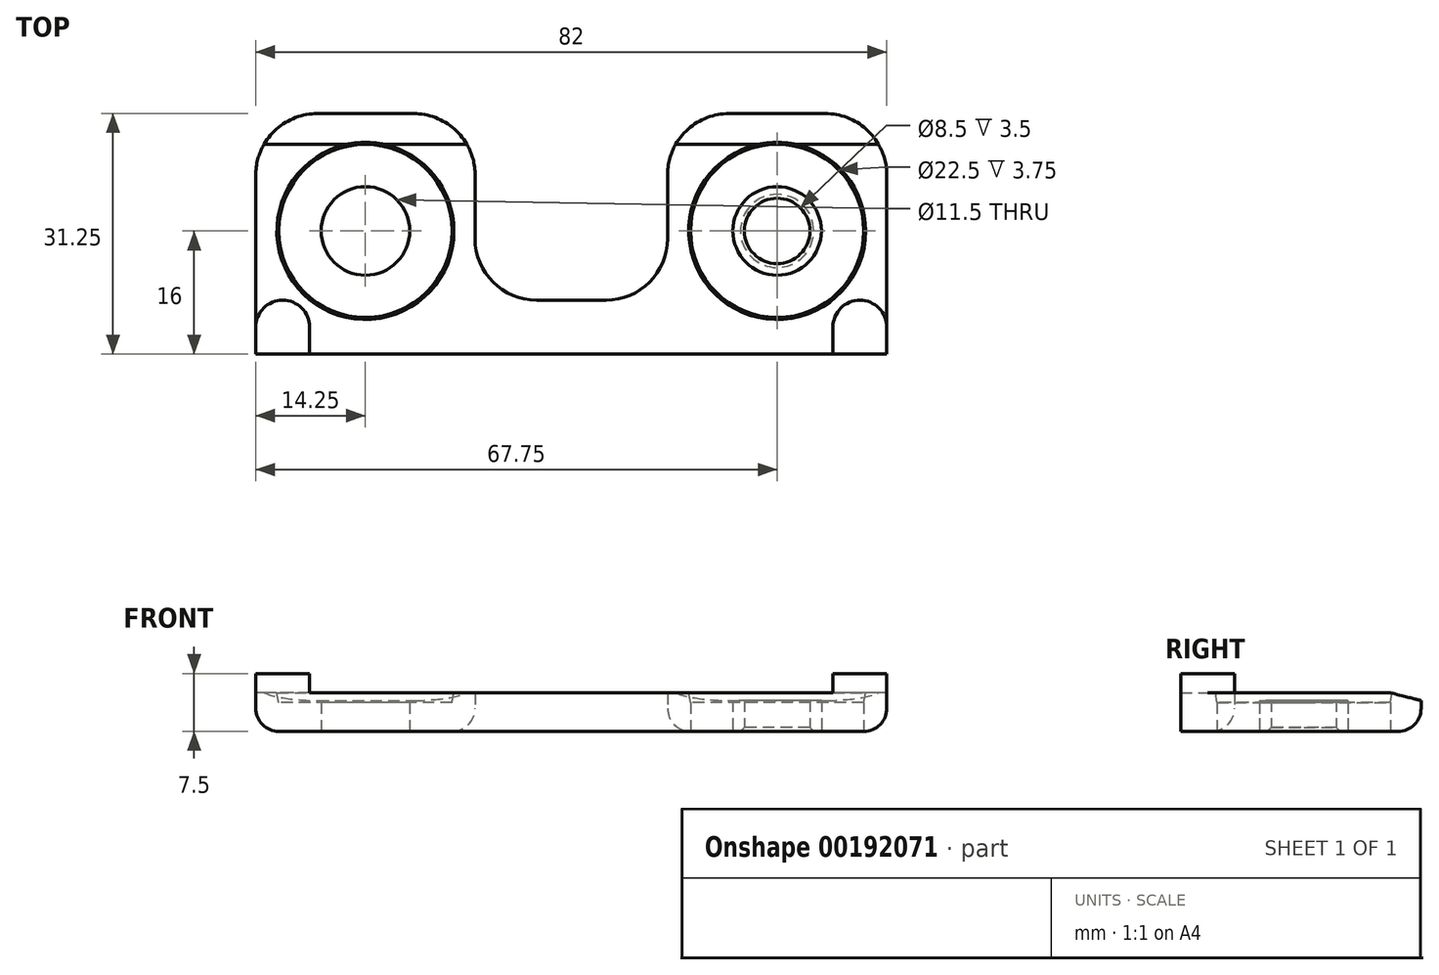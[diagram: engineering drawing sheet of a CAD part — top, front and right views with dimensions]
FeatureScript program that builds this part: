
annotation { "Feature Type Name" : "Feature", "Feature Type Description" : "" }
export const myFeature = defineFeature(function(context is Context, id is Id, definition is map)
    precondition{}
    {
        {
            var Q0;
            Q0=qCreatedBy(makeId("Top.planeOp"),FACE);
            var sketch = newSketch(context, id + "F0", { "sketchPlane" : qUnion([Q0])});
            skLineSegment(sketch, "E0.bottom", {"start": v(41, -3.5) * mm, "end": v(-41, -3.5) * mm});
            skLineSegment(sketch, "E0.top", {"start": v(12.5, 3.5) * mm, "end": v(-12.5, 3.5) * mm});
            skLineSegment(sketch, "E0.left", {"start": v(41, -3.5) * mm, "end": v(41, 3.5) * mm});
            skLineSegment(sketch, "E0.right", {"start": v(-41, -3.5) * mm, "end": v(-41, 3.5) * mm});
            skPoint(sketch, "E0.middle", {"position": v(0, 0) * mm});
            skLineSegment(sketch, "E1", {"start": v(-41, 3.5) * mm, "end": v(-41, 27.75) * mm});
            skLineSegment(sketch, "E2", {"start": v(-41, 27.75) * mm, "end": v(-12.5, 27.75) * mm});
            skLineSegment(sketch, "E3", {"start": v(-12.5, 27.75) * mm, "end": v(-12.5, 3.5) * mm});
            skCircle(sketch, "E4", {"center": v(-26.75, 12.5) * mm, "radius": 4.25 * mm});
            skLineSegment(sketch, "E5", {"start": v(-26.75, 18.7) * mm, "end": v(-26.75, 6.28) * mm, "construction": true});
            skLineSegment(sketch, "E6", {"start": v(0, -8.57) * mm, "end": v(0, 17) * mm, "construction": true});
            skLineSegment(sketch, "E7.MirrorCS", {"start": v(-41, 27.75) * mm, "end": v(-41, 3.5) * mm});
            skLineSegment(sketch, "E8.MirrorCS", {"start": v(-12.5, 3.5) * mm, "end": v(-12.5, 27.75) * mm});
            skLineSegment(sketch, "E9.MirrorCS", {"start": v(-12.5, 27.75) * mm, "end": v(-41, 27.75) * mm});
            skLineSegment(sketch, "E10.MirrorCS", {"start": v(12.5, 27.75) * mm, "end": v(12.5, 3.5) * mm});
            skCircle(sketch, "E11.MirrorC", {"center": v(26.75, 12.5) * mm, "radius": 4.25 * mm});
            skLineSegment(sketch, "E12.MirrorCS", {"start": v(12.5, 27.75) * mm, "end": v(41, 27.75) * mm});
            skLineSegment(sketch, "E13.MirrorCS", {"start": v(41, 27.75) * mm, "end": v(41, 3.5) * mm});
            skCircle(sketch, "E14", {"center": v(-26.75, 12.5) * mm, "radius": 11.25 * mm});
            skCircle(sketch, "E15.MirrorC", {"center": v(26.75, 12.5) * mm, "radius": 11.25 * mm});
            skCircle(sketch, "E16.0", {"center": v(-26.75, 12.5) * mm, "radius": 5.75 * mm});
            skCircle(sketch, "E17.MirrorC", {"center": v(26.75, 12.5) * mm, "radius": 5.75 * mm});
            skLineSegment(sketch, "E18", {"start": v(-41, 3.5) * mm, "end": v(-34, 3.5) * mm});
            skLineSegment(sketch, "E19", {"start": v(-34, 3.5) * mm, "end": v(-34, -3.5) * mm});
            skLineSegment(sketch, "E20.MirrorCS", {"start": v(34, 3.5) * mm, "end": v(34, -3.5) * mm});
            skLineSegment(sketch, "E21.MirrorCS", {"start": v(41, 3.5) * mm, "end": v(34, 3.5) * mm});
            skSolve(sketch);
        }
        {
            var Q0;
            Q0=makeQuery(id+"F0.imprint","IMPRINT",FACE,{"disambiguationData":[TD([[makeQuery(id+"F0.imprint","IMPRINT",EDGE,{"derivedFrom":sQuery(id+"F0.wireOp",EDGE,"E0.bottom")}),-1.0]])]});
            var Q1;
            Q1=makeQuery(id+"F0.imprint","IMPRINT",FACE,{"disambiguationData":[TD([[makeQuery(id+"F0.imprint","IMPRINT",EDGE,{"derivedFrom":sQuery(id+"F0.wireOp",EDGE,"E0.top")}),1.0]])]});
            extrude(context, id + "F1", {"entities" : qUnion([Q0, Q1]), "depth" : 5 * mm});
        }
        {
            var Q0;
            Q0=makeQuery(id+"F0.imprint","IMPRINT",FACE,{"disambiguationData":[TD([[makeQuery(id+"F0.imprint","IMPRINT",EDGE,{"derivedFrom":sQuery(id+"F0.wireOp",EDGE,"E14")}),1.0]])]});
            var Q1;
            Q1=makeQuery(id+"F0.imprint","IMPRINT",FACE,{"disambiguationData":[TD([[makeQuery(id+"F0.imprint","IMPRINT",EDGE,{"derivedFrom":sQuery(id+"F0.wireOp",EDGE,"E4")}),1.0]])]});
            var Q2;
            Q2=makeQuery(id+"F0.imprint","IMPRINT",FACE,{"disambiguationData":[TD([[makeQuery(id+"F0.imprint","IMPRINT",EDGE,{"derivedFrom":sQuery(id+"F0.wireOp",EDGE,"E15.MirrorC")}),-1.0]])]});
            var Q3;
            Q3=makeQuery(id+"F0.imprint","IMPRINT",FACE,{"disambiguationData":[TD([[makeQuery(id+"F0.imprint","IMPRINT",EDGE,{"derivedFrom":sQuery(id+"F0.wireOp",EDGE,"E11.MirrorC")}),-1.0]])]});
            extrude(context, id + "F2", {"entities" : qUnion([Q0, Q1, Q2, Q3]), "operationType" : NewBodyOperationType.ADD, "depth" : 3.75 * mm});
        }
        {
            var Q0;
            Q0=makeQuery(id+"F0.imprint","IMPRINT",FACE,{"disambiguationData":[TD([[makeQuery(id+"F0.imprint","IMPRINT",EDGE,{"derivedFrom":sQuery(id+"F0.wireOp",EDGE,"E4")}),1.0]])]});
            var Q1;
            Q1=makeQuery(id+"F0.imprint","IMPRINT",FACE,{"disambiguationData":[TD([[makeQuery(id+"F0.imprint","IMPRINT",EDGE,{"derivedFrom":sQuery(id+"F0.wireOp",EDGE,"E11.MirrorC")}),-1.0]])]});
            extrude(context, id + "F3", {"entities" : qUnion([Q0, Q1]), "operationType" : NewBodyOperationType.ADD, "depth" : 4 * mm});
        }
        {
            var Q0;
            {var subQ0=sQuery(id+"F0.wireOp",EDGE,"E0.right");Q0=makeQuery(id+"F0.imprint","IMPRINT",FACE,{"disambiguationData":[TD([[makeQuery(id+"F0.imprint","IMPRINT",EDGE,{"derivedFrom":subQ0}),-1.0]])]});}
            var Q1;
            {var subQ0=sQuery(id+"F0.wireOp",EDGE,"E0.left");Q1=makeQuery(id+"F0.imprint","IMPRINT",FACE,{"disambiguationData":[TD([[makeQuery(id+"F0.imprint","IMPRINT",EDGE,{"derivedFrom":subQ0}),1.0]])]});}
            extrude(context, id + "F4", {"entities" : qUnion([Q0, Q1]), "operationType" : NewBodyOperationType.ADD, "depth" : 7.5 * mm});
        }
        {
            var Q0;
            Q0=makeQuery(id+"F1.opExtrude","SWEPT_EDGE",EDGE,{"disambiguationData":[OSD([sQuery(id+"F0.wireOp",EDGE,"E0.top"),sQuery(id+"F0.wireOp",EDGE,"E3")])]});
            var Q1;
            Q1=makeQuery(id+"F1.opExtrude","SWEPT_EDGE",EDGE,{"disambiguationData":[OSD([sQuery(id+"F0.wireOp",EDGE,"E0.top"),sQuery(id+"F0.wireOp",EDGE,"E10.MirrorCS")])]});
            var Q2;
            Q2=makeQuery(id+"F1.opExtrude","SWEPT_EDGE",EDGE,{"disambiguationData":[OSD([sQuery(id+"F0.wireOp",EDGE,"E10.MirrorCS"),sQuery(id+"F0.wireOp",EDGE,"E12.MirrorCS")])]});
            var Q3;
            Q3=makeQuery(id+"F1.opExtrude","SWEPT_EDGE",EDGE,{"disambiguationData":[OSD([sQuery(id+"F0.wireOp",EDGE,"E12.MirrorCS"),sQuery(id+"F0.wireOp",EDGE,"E13.MirrorCS")])]});
            var Q4;
            Q4=makeQuery(id+"F1.opExtrude","SWEPT_EDGE",EDGE,{"disambiguationData":[OSD([sQuery(id+"F0.wireOp",EDGE,"E7.MirrorCS"),sQuery(id+"F0.wireOp",EDGE,"E2")])]});
            var Q5;
            Q5=makeQuery(id+"F1.opExtrude","SWEPT_EDGE",EDGE,{"disambiguationData":[OSD([sQuery(id+"F0.wireOp",EDGE,"E2"),sQuery(id+"F0.wireOp",EDGE,"E3")])]});
            fillet(context, id + "F5", {"entities" : qUnion([Q0, Q1, Q2, Q3, Q4, Q5]), "radius" : 8 * mm, "tangentPropagation" : true, "allowEdgeOverflow" : false});
        }
        {
            var Q0;
            Q0=makeQuery(id+"F1.opExtrude","CAP_EDGE",EDGE,{"disambiguationData":[OSD([sQuery(id+"F0.wireOp",EDGE,"E2")])],"isStart":false});
            var Q1;
            Q1=makeQuery(id+"F1.opExtrude","CAP_EDGE",EDGE,{"disambiguationData":[OSD([sQuery(id+"F0.wireOp",EDGE,"E12.MirrorCS")])],"isStart":false});
            chamfer(context, id + "F6", {"entities" : qUnion([Q0, Q1]), "chamferType" : ChamferType.TWO_OFFSETS, "width1" : 1 * mm, "oppositeDirection" : false, "width2" : 4 * mm});
        }
        {
            var Q0;
            Q0=makeQuery(id+"F1.opExtrude","CAP_EDGE",EDGE,{"disambiguationData":[OSD([sQuery(id+"F0.wireOp",EDGE,"E2")])],"isStart":true});
            fillet(context, id + "F7", {"entities" : qUnion([Q0]), "radius" : 3 * mm, "tangentPropagation" : true, "allowEdgeOverflow" : false});
        }
        {
            var Q0;
            Q0=makeQuery(id+"F4.opExtrude","SWEPT_EDGE",EDGE,{"disambiguationData":[OSD([sQuery(id+"F0.wireOp",EDGE,"E18"),sQuery(id+"F0.wireOp",EDGE,"E19")])]});
            var Q1;
            Q1=makeQuery(id+"F4.opExtrude","SWEPT_EDGE",EDGE,{"disambiguationData":[OSD([sQuery(id+"F0.wireOp",EDGE,"E0.right"),sQuery(id+"F0.wireOp",EDGE,"E7.MirrorCS"),sQuery(id+"F0.wireOp",EDGE,"E18")])]});
            var Q2;
            Q2=makeQuery(id+"F4.opExtrude","SWEPT_EDGE",EDGE,{"disambiguationData":[OSD([sQuery(id+"F0.wireOp",EDGE,"E20.MirrorCS"),sQuery(id+"F0.wireOp",EDGE,"E21.MirrorCS")])]});
            var Q3;
            Q3=makeQuery(id+"F4.opExtrude","SWEPT_EDGE",EDGE,{"disambiguationData":[OSD([sQuery(id+"F0.wireOp",EDGE,"E0.left"),sQuery(id+"F0.wireOp",EDGE,"E13.MirrorCS"),sQuery(id+"F0.wireOp",EDGE,"E21.MirrorCS")])]});
            fillet(context, id + "F8", {"entities" : qUnion([Q0, Q1, Q2, Q3]), "radius" : 3.5 * mm, "tangentPropagation" : true, "allowEdgeOverflow" : false});
        }
        {
            var Q0;
            Q0=makeQuery(id+"F1.opExtrude","CAP_EDGE",EDGE,{"disambiguationData":[OSD([sQuery(id+"F0.wireOp",EDGE,"E14")])],"isStart":false});
            var Q1;
            Q1=makeQuery(id+"F1.opExtrude","CAP_EDGE",EDGE,{"disambiguationData":[OSD([sQuery(id+"F0.wireOp",EDGE,"E15.MirrorC")])],"isStart":false});
            chamfer(context, id + "F9", {"entities" : qUnion([Q0, Q1]), "chamferType" : ChamferType.TWO_OFFSETS, "width1" : 1.25 * mm, "oppositeDirection" : false, "width2" : .25 * mm, "tangentPropagation" : true});
        }
        {
            var Q0;
            Q0=makeQuery(id+"F2.opExtrude","CAP_EDGE",EDGE,{"disambiguationData":[OSD([sQuery(id+"F0.wireOp",EDGE,"E11.MirrorC")])],"isStart":true});
            var Q1;
            Q1=makeQuery(id+"F2.opExtrude","CAP_EDGE",EDGE,{"disambiguationData":[OSD([sQuery(id+"F0.wireOp",EDGE,"E4")])],"isStart":true});
            chamfer(context, id + "F10", {"entities" : qUnion([Q0, Q1]), "width" : .5 * mm, "tangentPropagation" : true});
        }
    });
